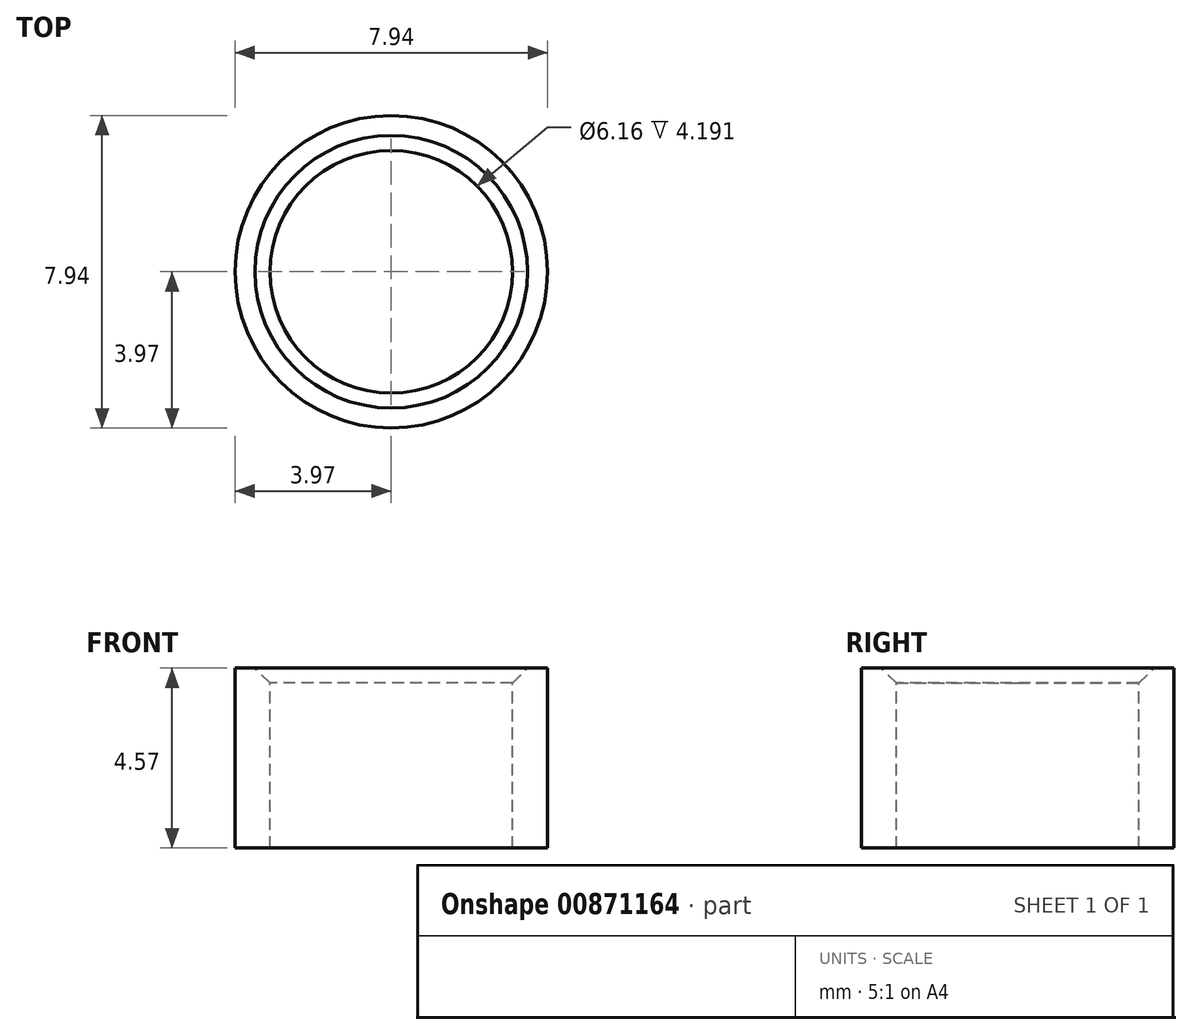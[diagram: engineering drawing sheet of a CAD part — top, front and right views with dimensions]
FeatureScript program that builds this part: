
annotation { "Feature Type Name" : "Feature", "Feature Type Description" : "" }
export const myFeature = defineFeature(function(context is Context, id is Id, definition is map)
    precondition{}
    {
        {
            var Q0;
            Q0=qCreatedBy(makeId("Top.planeOp"),FACE);
            var sketch = newSketch(context, id + "F0", { "sketchPlane" : qUnion([Q0])});
            skCircle(sketch, "E0", {"center": v(0, 0) * mm, "radius": 3.97 * mm});
            skCircle(sketch, "E1.0", {"center": v(0, 0) * mm, "radius": 3.08 * mm});
            skSolve(sketch);
        }
        {
            var Q0;
            Q0=makeQuery(id+"F0.imprint","IMPRINT",FACE,{"disambiguationData":[TD([[makeQuery(id+"F0.imprint","IMPRINT",EDGE,{"derivedFrom":sQuery(id+"F0.wireOp",EDGE,"E0")}),1.0]])]});
            extrude(context, id + "F1", {"entities" : qUnion([Q0]), "oppositeDirection" : true, "depth" : 4.57 * mm, "offsetDistance" : 25.4 * mm});
        }
        {
            var Q0;
            Q0=makeQuery(id+"F1.opExtrude","CAP_EDGE",EDGE,{"disambiguationData":[OSD([sQuery(id+"F0.wireOp",EDGE,"E1.0")])],"isStart":true});
            chamfer(context, id + "F2", {"entities" : qUnion([Q0]), "width" : 0.38 * mm, "tangentPropagation" : true});
        }
    });
